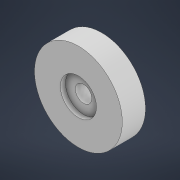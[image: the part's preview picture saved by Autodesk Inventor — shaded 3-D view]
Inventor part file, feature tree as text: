
AUTODESK INVENTOR PART (.ipt)
format: ipt  version: 2021 (Build 250183000, 183)  size: 242,176 bytes
history: native  units: mm
features: extrude x4, sketch x4, other x1
ambient origin geometry x8: Origin, YZ Plane, XZ Plane, XY Plane, X Axis, Y Axis, Z Axis, Center Point
bodies: Volumenkörper1 (feature_tree)
feature tree (9):
  other  "Boogie_gegenstück"
  extrude  "Extrusion1"  Depth=4.5mm TaperAngle=0.0deg
  extrude  "Extrusion2"  Depth=1.0mm TaperAngle=0.0deg
  extrude  "Extrusion3"  Depth=1.0mm TaperAngle=0.0deg
  extrude  "Extrusion4"  Depth=1.0mm TaperAngle=0.0deg
  sketch  "Skizze1"  dims[d0=17.0mm d1=4.5mm d2=0.0mm]
  sketch  "Skizze2"  dims[d3=15.0mm d4=1.0mm d5=0.0mm]
  sketch  "Skizze3"  dims[d6=7.0mm d7=1.0mm d8=0.0mm]
  sketch  "Skizze4"  dims[d9=3.2mm d10=1.0mm d11=0.0mm]
